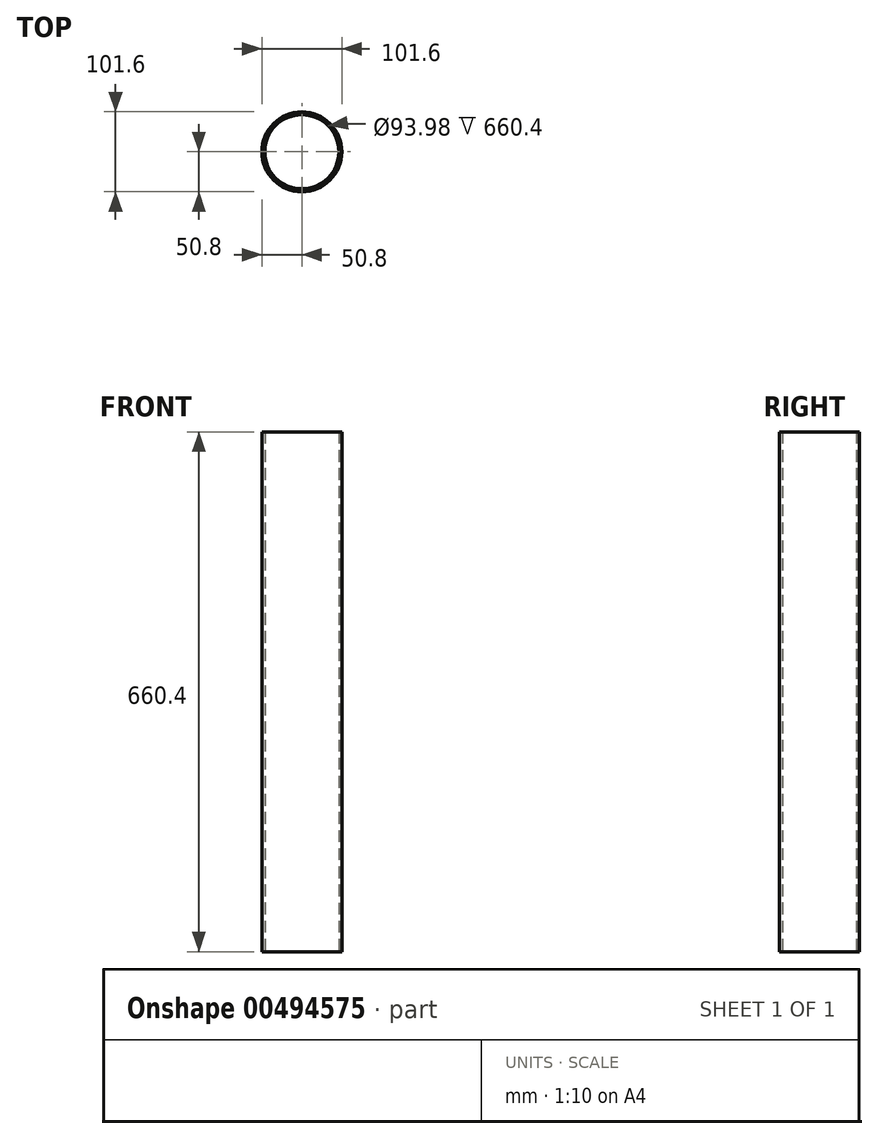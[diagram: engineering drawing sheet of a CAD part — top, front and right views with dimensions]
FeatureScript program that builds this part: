
annotation { "Feature Type Name" : "Feature", "Feature Type Description" : "" }
export const myFeature = defineFeature(function(context is Context, id is Id, definition is map)
    precondition{}
    {
        {
            var Q0;
            Q0=qCreatedBy(makeId("Top.planeOp"),FACE);
            var sketch = newSketch(context, id + "F0", { "sketchPlane" : qUnion([Q0])});
            skCircle(sketch, "E0", {"center": v(0, 0) * mm, "radius": 50.8 * mm});
            skSolve(sketch);
        }
        {
            var Q0;
            Q0 = qSketchRegion(id + "F0", true);
            extrude(context, id + "F1", {"entities" : qUnion([Q0]), "depth" : 660.4 * mm});
        }
        {
            var Q0;
            Q0=makeQuery(id+"F1.opExtrude","CAP_FACE",FACE,{"disambiguationData":[OSD([sQuery(id+"F0.wireOp",EDGE,"E0")])],"isStart":true});
            shell(context, id + "F2", {"entities" : qUnion([Q0]), "thickness" : 3.8 * mm});
        }
        {
            var Q0;
            Q0=makeQuery(id+"F1.opExtrude","CAP_FACE",FACE,{"disambiguationData":[OSD([sQuery(id+"F0.wireOp",EDGE,"E0")])],"isStart":true});
            var sketch = newSketch(context, id + "F3", { "sketchPlane" : qUnion([Q0])});
            skCircle(sketch, "E1", {"center": v(0, 0) * mm, "radius": 46.99 * mm});
            skSolve(sketch);
        }
        {
            var Q0;
            Q0 = qSketchRegion(id + "F3", true);
            extrude(context, id + "F4", {"entities" : qUnion([Q0]), "operationType" : NewBodyOperationType.REMOVE, "endBound" : BoundingType.THROUGH_ALL, "oppositeDirection" : true, "depth" : 25.4 * mm});
        }
    });
